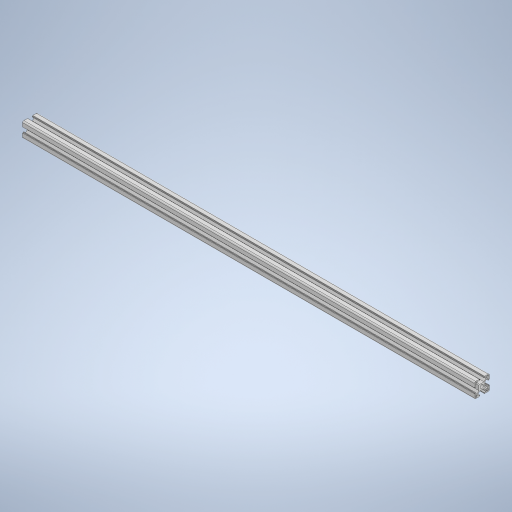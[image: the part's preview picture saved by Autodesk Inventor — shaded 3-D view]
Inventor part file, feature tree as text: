
AUTODESK INVENTOR PART (.ipt)
format: ipt  version: 2023 (Build 270158000, 158)  size: 373,760 bytes
history: native  units: mm
features: extrude x1, mirror x1, pattern_circular x1, sketch x1
ambient origin geometry x8: Origin, YZ Plane, XZ Plane, XY Plane, X Axis, Y Axis, Z Axis, Center Point
bodies: Solid1 (feature_tree)
feature tree (4):
  extrude  "Extrusion1"  TaperAngle=45.0deg  [1 undecoded]
  mirror  "Mirror1"
  pattern_circular  "Circular Pattern1"  Angle=45.0deg  [1 undecoded]
  sketch  "Sketch1"  dims[d0=3.4mm d1=45.0deg d3=45.0deg d4=2.5mm d5=135.0deg d6=1.0mm d7=4.1mm d8=5.2mm d9=8.25mm d10=15.0mm d11=2.2mm d12=5.8mm d13=1.5mm d14=1.5mm d15=1.0mm d16=1.0mm d17=1.0mm d18=900.0mm d19=0.0mm d20=40.0mm d21=360.0deg]
note: 2 required parameter values undecoded (feature->parameter linkage not recoverable at this tier; creation-order binding heuristic only, values carry confidence <= 0.55)
